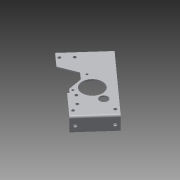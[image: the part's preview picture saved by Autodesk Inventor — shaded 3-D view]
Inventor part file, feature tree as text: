
AUTODESK INVENTOR PART (.ipt)
format: ipt  version: 2013 (Build 170138000, 138)  size: 516,608 bytes
history: native  units: in
note: dims shown in document units (in); Inventor stores cm internally (conversion verified against a paired STEP export)
features: sheet_metal_op x25, other x24, sketch x23, reference x1, extrude x1
ambient origin geometry x8: Origin, YZ Plane, XZ Plane, XY Plane, X Axis, Y Axis, Z Axis, Center Point
feature tree (74):
  sheet_metal_op  "Face2"
  sheet_metal_op  "Face5"
  sheet_metal_op  "Face6"
  sheet_metal_op  "Face7"
  sheet_metal_op  "Flange4"
  sheet_metal_op  "Flange5"
  sheet_metal_op  "Face8"
  sheet_metal_op  "Face9"
  sheet_metal_op  "Flange6"
  sheet_metal_op  "Flange7"
  sheet_metal_op  "Face13"
  sketch  "Sketch1"  dims[d8=0.125in]
  other  "Plate3"
  sketch  "Sketch8"  dims[d19=1.875in d20=0.375in d21=0.375in d22=0.375in d23=1.125in d24=1.6742in d25=1.6742in d26=1.8904in d27=0.3in d28=0.3in d29=0.3in d30=0.3in d31=0.125in]
  sketch  "Sketch9"  dims[d32=1.0in]
  other  "Plate8"
  sheet_metal_op  "Bend6"
  sketch  "Sketch10"  dims[d33=1.25in]
  sketch  "Sketch11"  dims[d86=2.0in]
  other  "Plate9"
  sheet_metal_op  "Bend7"
  sketch  "Sketch12"  dims[d87=0.125in]
  sketch  "Sketch14"  dims[d88=0.0in]
  sketch  "Sketch15"  dims[d89=3.0in]
  other  "Plate10"
  sheet_metal_op  "Bend8"
  sketch  "Sketch16"  dims[d90=0.125in]
  other  "Plate11"
  sheet_metal_op  "Bend9"
  sheet_metal_op  "Corner4"
  sketch  "Sketch17"  dims[d91=0.125in]
  other  "Plate12"
  sheet_metal_op  "Bend10"
  sheet_metal_op  "Corner5"
  sketch  "Sketch18"  dims[d92=0.0625in]
  sketch  "Sketch19"  dims[d93=0.25in]
  sketch  "Sketch20"  dims[d94=0.125in]
  reference  "Reference4"
  sketch  "Sketch21"  dims[d95=0.266in]
  sketch  "Sketch22"  dims[d96=0.266in]
  sketch  "Sketch23"  dims[d97=2.75in]
  other  "Plate13"
  sheet_metal_op  "Bend11"
  sketch  "Sketch24"  dims[d98=0.3125in]
  sketch  "Sketch25"  dims[d99=0.5in]
  sketch  "Sketch26"  dims[d100=0.5in]
  other  "Plate14"
  sheet_metal_op  "Bend12"
  sketch  "Sketch27"  dims[d101=0.125in]
  other  "Plate15"
  sheet_metal_op  "Bend13"
  sheet_metal_op  "Corner6"
  sketch  "Sketch28"  dims[d102=0.0in]
  other  "Plate16"
  sheet_metal_op  "Bend14"
  sheet_metal_op  "Corner7"
  sketch  "Sketch38"  dims[d103=3.875in]
  sketch  "Sketch39"  dims[d104=2.375in d105=0.125in d106=0.125in d107=0.0625in d108=0.25in d109=0.125in d110=0.266in d111=0.266in d112=0.5in d113=0.375in d114=1.5in d115=0.5in d116=0.125in d117=0.0in d124=0.0625in d126=0.125in d127=0.0in d128=0.2in d130=0.2in d131=0.2in d132=0.125in d133=0.125in d134=0.0625in d135=0.25in d136=0.125in d137=0.125in d138=0.0625in d139=0.25in d140=0.125in d141=1.25in d142=90.0deg d143=0.05in d144=0.5in d145=0.125in d146=0.125in d147=0.125in d148=0.0625in d149=0.25in d150=0.125in d151=1.25in d152=90.0deg d153=0.05in d154=0.5in d155=0.125in d156=0.125in d157=0.266in d158=0.266in d159=0.5in d160=0.375in d161=0.375in d162=0.5in d163=100.0in d164=0.0in d165=0.266in d166=0.375in d167=0.5in d168=0.125in d169=0.0in d171=0.748in d172=1.0in d173=24.0in d174=0.125in d175=0.0in d176=1.75in d177=0.5in d178=1.0in d179=0.266in d180=0.266in d181=0.125in d182=0.0in d183=0.2in d184=0.0687in d186=1.2992in d187=1.2992in d188=0.2in d189=0.0687in d190=1.2992in d191=1.2992in d192=0.2in d193=0.0687in d194=1.5154in d195=1.5154in d196=0.125in d197=0.0in d198=0.125in d199=0.125in d200=0.0625in d201=0.25in d202=0.125in d203=2.5in d204=0.125in d205=0.0in d206=0.25in d207=0.125in d208=0.0in d209=1.5in d210=2.25in d211=0.125in d212=0.125in d213=0.0625in d214=0.25in d215=0.125in d216=1.5in d217=0.125in d218=0.0625in d219=0.25in d220=0.125in d221=1.25in d222=90.0deg d223=0.05in d224=0.5in d225=0.125in d226=0.125in d227=0.125in d228=0.0625in d229=0.25in d230=0.125in d231=1.25in d232=90.0deg d233=0.05in d234=0.5in d235=0.125in d236=0.125in d270=90.0deg d272=0.375in d302=0.266in d303=0.266in d304=1.0in d305=0.25in d306=0.125in d307=0.0in d308=0.125in d309=0.125in d310=0.0625in d311=0.25in d312=0.125in d0=0.125in d1=0.0625in d2=0.25in d3=0.125in d5=0.125in d6=0.0625in d7=0.25in d9=0.0in d10=0.125in d11=0.0625in d12=0.25in d13=0.125in d14=0.25in d15=0.125in d16=0.0625in d17=0.125in d18=1.0in]
  other  "Plate22"
  sheet_metal_op  "Bend20"
  other  "Cut2"
  other  "Cut3"
  other  "Cut4"
  other  "Cut6"
  other  "Cut7"
  other  "Cut8"
  other  "Cut9"
  other  "Cut10"
  other  "Cut11"
  other  "Cut12"
  other  "Cut13"
  other  "Cut18"
  other  "Definition1"
  extrude  "Extrusion1"  Depth=0.125in
